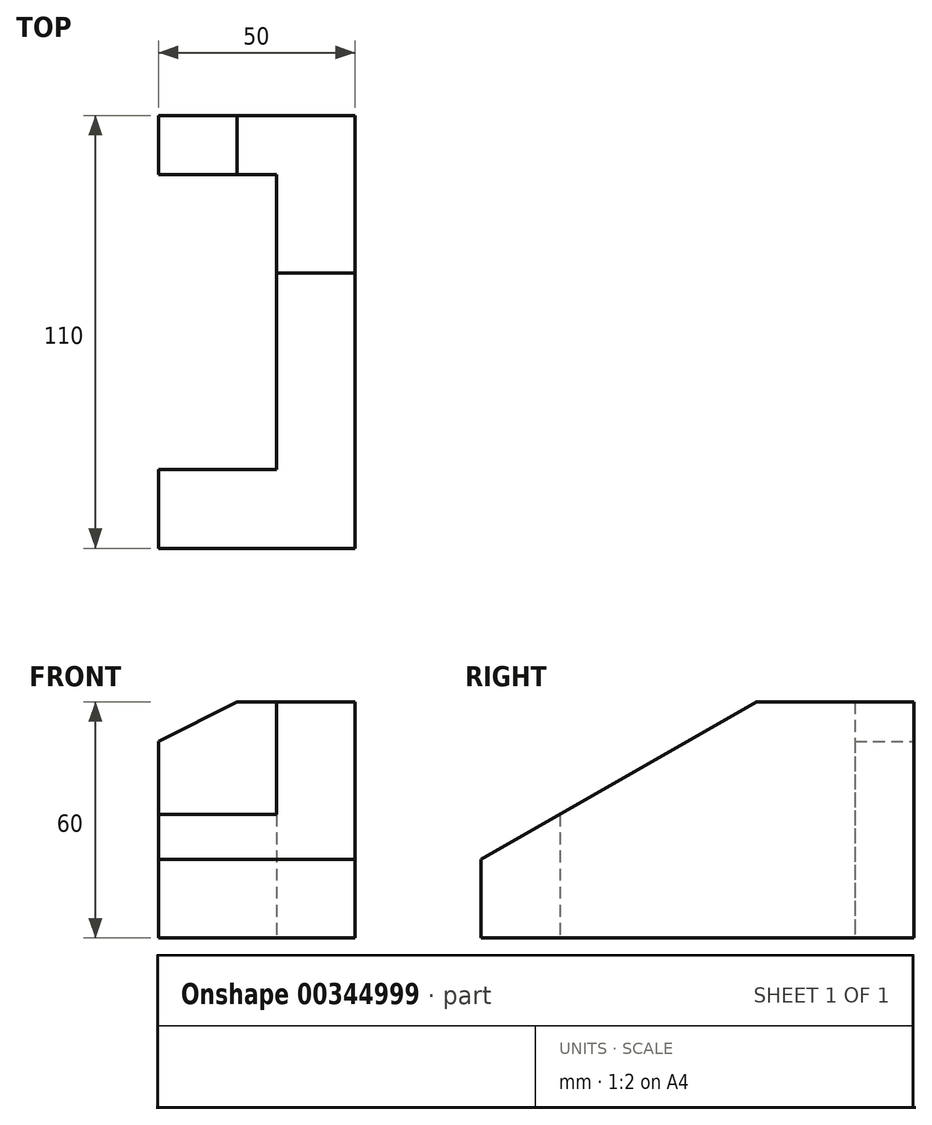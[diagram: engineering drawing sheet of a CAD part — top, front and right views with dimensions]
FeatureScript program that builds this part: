
annotation { "Feature Type Name" : "Feature", "Feature Type Description" : "" }
export const myFeature = defineFeature(function(context is Context, id is Id, definition is map)
    precondition{}
    {
        {
            var Q0;
            Q0=qCreatedBy(makeId("Top.planeOp"),FACE);
            var sketch = newSketch(context, id + "F0", { "sketchPlane" : qUnion([Q0])});
            skLineSegment(sketch, "E0.bottom", {"start": v(25, -55) * mm, "end": v(-25, -55) * mm});
            skLineSegment(sketch, "E0.top", {"start": v(25, 55) * mm, "end": v(-25, 55) * mm});
            skLineSegment(sketch, "E0.left", {"start": v(25, -55) * mm, "end": v(25, 55) * mm});
            skLineSegment(sketch, "E0.right", {"start": v(-25, -55) * mm, "end": v(-25, 55) * mm});
            skPoint(sketch, "E0.middle", {"position": v(0, 0) * mm});
            skLineSegment(sketch, "E1", {"start": v(5, 55) * mm, "end": v(5, 40) * mm, "construction": true});
            skLineSegment(sketch, "E2", {"start": v(5, 40) * mm, "end": v(-25, 40) * mm});
            skLineSegment(sketch, "E3", {"start": v(5, 40) * mm, "end": v(5, -35) * mm});
            skLineSegment(sketch, "E4", {"start": v(5, -35) * mm, "end": v(-25, -35) * mm});
            skSolve(sketch);
        }
        {
            var Q0;
            {var subQ1=sQuery(id+"F0.wireOp",EDGE,"E0.bottom");Q0=makeQuery(id+"F0.imprint","IMPRINT",FACE,{"disambiguationData":[TD([[makeQuery(id+"F0.imprint","IMPRINT",EDGE,{"derivedFrom":subQ1}),-1.0]])]});}
            extrude(context, id + "F1", {"entities" : qUnion([Q0]), "depth" : 60 * mm});
        }
        {
            var Q0;
            Q0=makeQuery(id+"F1.opExtrude","SWEPT_FACE",FACE,{"disambiguationData":[OSD([sQuery(id+"F0.wireOp",EDGE,"E0.left")])]});
            var sketch = newSketch(context, id + "F2", { "sketchPlane" : qUnion([Q0])});
            skLineSegment(sketch, "E5", {"start": v(-55, 20) * mm, "end": v(15, 60) * mm});
            skLineSegment(sketch, "E6.0", {"start": v(-55, 60) * mm, "end": v(-55, 20) * mm});
            skPoint(sketch, "E7.orphan", {"position": v(55, 60) * mm});
            skPoint(sketch, "E8.orphan", {"position": v(-55, 0) * mm});
            skSolve(sketch);
        }
        {
            var Q0;
            {var subQ0=sQuery(id+"F2.wireOp",EDGE,"E5");Q0=makeQuery(id+"F2.imprint","IMPRINT",FACE,{"disambiguationData":[TD([[makeQuery(id+"F2.imprint","IMPRINT",EDGE,{"derivedFrom":subQ0}),1.0]])]});}
            extrude(context, id + "F3", {"entities" : qUnion([Q0]), "operationType" : NewBodyOperationType.REMOVE, "oppositeDirection" : true, "depth" : 60 * mm});
        }
        {
            var Q0;
            Q0=makeQuery(id+"F1.opExtrude","SWEPT_FACE",FACE,{"disambiguationData":[OSD([sQuery(id+"F0.wireOp",EDGE,"E0.top")])]});
            var sketch = newSketch(context, id + "F4", { "sketchPlane" : qUnion([Q0])});
            skLineSegment(sketch, "E9", {"start": v(5, 60) * mm, "end": v(25, 50) * mm});
            skLineSegment(sketch, "E10.0", {"start": v(25, 60) * mm, "end": v(25, 0) * mm});
            skLineSegment(sketch, "E11.0", {"start": v(-25, 60) * mm, "end": v(25, 60) * mm});
            skSolve(sketch);
        }
        {
            var Q0;
            {var subQ0=sQuery(id+"F4.wireOp",EDGE,"E9");Q0=makeQuery(id+"F4.imprint","IMPRINT",FACE,{"disambiguationData":[TD([[makeQuery(id+"F4.imprint","IMPRINT",EDGE,{"derivedFrom":subQ0}),1.0]])]});}
            extrude(context, id + "F5", {"entities" : qUnion([Q0]), "operationType" : NewBodyOperationType.REMOVE, "oppositeDirection" : true, "depth" : 15 * mm});
        }
    });
